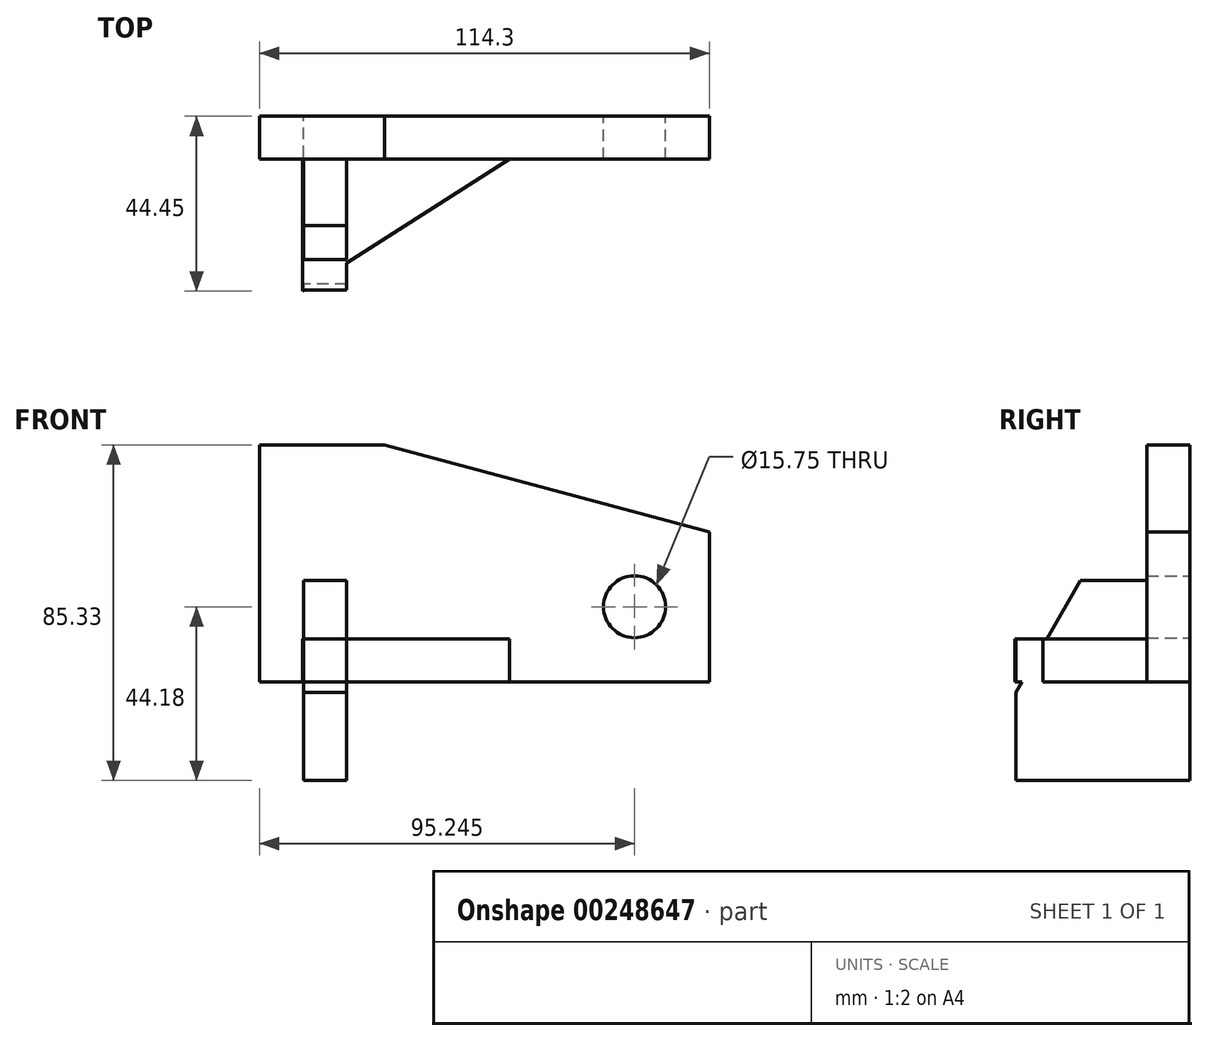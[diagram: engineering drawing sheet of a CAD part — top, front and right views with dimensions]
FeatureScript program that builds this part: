
annotation { "Feature Type Name" : "Feature", "Feature Type Description" : "" }
export const myFeature = defineFeature(function(context is Context, id is Id, definition is map)
    precondition{}
    {
        {
            var Q0;
            Q0=qCreatedBy(makeId("Front.planeOp"),FACE);
            var sketch = newSketch(context, id + "F0", { "sketchPlane" : qUnion([Q0])});
            skLineSegment(sketch, "E0", {"start": v(-95.02, -19.27) * mm, "end": v(19.28, -19.27) * mm});
            skLineSegment(sketch, "E1", {"start": v(-95.02, -19.27) * mm, "end": v(-95.02, 40.93) * mm});
            skLineSegment(sketch, "E2", {"start": v(-95.02, 40.93) * mm, "end": v(-63.27, 40.93) * mm});
            skLineSegment(sketch, "E3", {"start": v(19.28, -19.27) * mm, "end": v(19.28, 18.8) * mm});
            skLineSegment(sketch, "E4", {"start": v(19.28, 18.8) * mm, "end": v(-63.27, 40.93) * mm});
            skCircle(sketch, "E5", {"center": v(0.23, -0.22) * mm, "radius": 7.87 * mm});
            skSolve(sketch);
        }
        {
            var Q0;
            Q0=makeQuery(id+"F0.imprint","IMPRINT",FACE,{"disambiguationData":[TD([[makeQuery(id+"F0.imprint","IMPRINT",EDGE,{"derivedFrom":sQuery(id+"F0.wireOp",EDGE,"E0")}),1.0]])]});
            extrude(context, id + "F1", {"entities" : qUnion([Q0]), "depth" : 10.92 * mm});
        }
        {
            var Q0;
            Q0=makeQuery(id+"F1.opExtrude","SWEPT_FACE",FACE,{"disambiguationData":[OSD([sQuery(id+"F0.wireOp",EDGE,"E0")])]});
            var sketch = newSketch(context, id + "F2", { "sketchPlane" : qUnion([Q0])});
            skLineSegment(sketch, "E6", {"start": v(-95.02, 44.45) * mm, "end": v(-84.1, 44.45) * mm});
            skLineSegment(sketch, "E7", {"start": v(-84.1, 44.45) * mm, "end": v(-31.52, 10.92) * mm});
            skLineSegment(sketch, "E8", {"start": v(-95.02, 44.45) * mm, "end": v(-95.02, 0) * mm});
            skLineSegment(sketch, "E9", {"start": v(-84.1, 44.45) * mm, "end": v(-84.1, 10.92) * mm});
            skSolve(sketch);
        }
        {
            var Q0;
            {var subQ0=sQuery(id+"F2.wireOp",EDGE,"E7");Q0=makeQuery(id+"F2.imprint","IMPRINT",FACE,{"disambiguationData":[TD([[makeQuery(id+"F2.imprint","IMPRINT",EDGE,{"derivedFrom":subQ0}),-1.0]])]});}
            extrude(context, id + "F3", {"entities" : qUnion([Q0]), "operationType" : NewBodyOperationType.ADD, "oppositeDirection" : true, "depth" : 10.92 * mm});
        }
        {
            var Q0;
            Q0=qCreatedBy(makeId("Front.planeOp"),FACE);
            var sketch = newSketch(context, id + "F4", { "sketchPlane" : qUnion([Q0])});
            skLineSegment(sketch, "E10.bottom", {"start": v(-83.8, 6.4) * mm, "end": v(-72.88, 6.4) * mm});
            skLineSegment(sketch, "E10.top", {"start": v(-83.8, -44.4) * mm, "end": v(-72.88, -44.4) * mm});
            skLineSegment(sketch, "E10.left", {"start": v(-83.8, 6.4) * mm, "end": v(-83.8, -44.4) * mm});
            skLineSegment(sketch, "E10.right", {"start": v(-72.88, 6.4) * mm, "end": v(-72.88, -44.4) * mm});
            skSolve(sketch);
        }
        {
            var Q0;
            Q0 = qSketchRegion(id + "F4", true);
            extrude(context, id + "F5", {"entities" : qUnion([Q0]), "operationType" : NewBodyOperationType.ADD, "depth" : 44.45 * mm});
        }
        {
            var Q0;
            Q0=makeQuery(id+"F5.opExtrude","SWEPT_FACE",FACE,{"disambiguationData":[OSD([sQuery(id+"F4.wireOp",EDGE,"E10.left")])]});
            var sketch = newSketch(context, id + "F6", { "sketchPlane" : qUnion([Q0])});
            skLineSegment(sketch, "E11", {"start": v(27.81, 6.4) * mm, "end": v(44.39, -22.3) * mm});
            skLineSegment(sketch, "E12", {"start": v(27.81, 6.4) * mm, "end": v(44.45, 6.4) * mm});
            skLineSegment(sketch, "E13", {"start": v(44.39, -22.3) * mm, "end": v(44.45, 6.4) * mm});
            skSolve(sketch);
        }
        {
            var Q0;
            Q0=makeQuery(id+"F6.imprint","IMPRINT",FACE,{"disambiguationData":[TD([[makeQuery(id+"F6.imprint","IMPRINT",EDGE,{"derivedFrom":sQuery(id+"F6.wireOp",EDGE,"E11")}),1.0]])]});
            extrude(context, id + "F7", {"entities" : qUnion([Q0]), "operationType" : NewBodyOperationType.REMOVE, "oppositeDirection" : true, "depth" : 25.4 * mm});
        }
        {
            var Q0;
            Q0=makeQuery(id+"F5.opExtrude","CAP_FACE",FACE,{"disambiguationData":[OSD([sQuery(id+"F4.wireOp",EDGE,"E10.bottom"),sQuery(id+"F4.wireOp",EDGE,"E10.top"),sQuery(id+"F4.wireOp",EDGE,"E10.left"),sQuery(id+"F4.wireOp",EDGE,"E10.right")])],"isStart":false});
            extrude(context, id + "F8", {"entities" : qUnion([Q0]), "operationType" : NewBodyOperationType.REMOVE, "oppositeDirection" : true, "depth" : 0.25 * mm});
        }
    });
